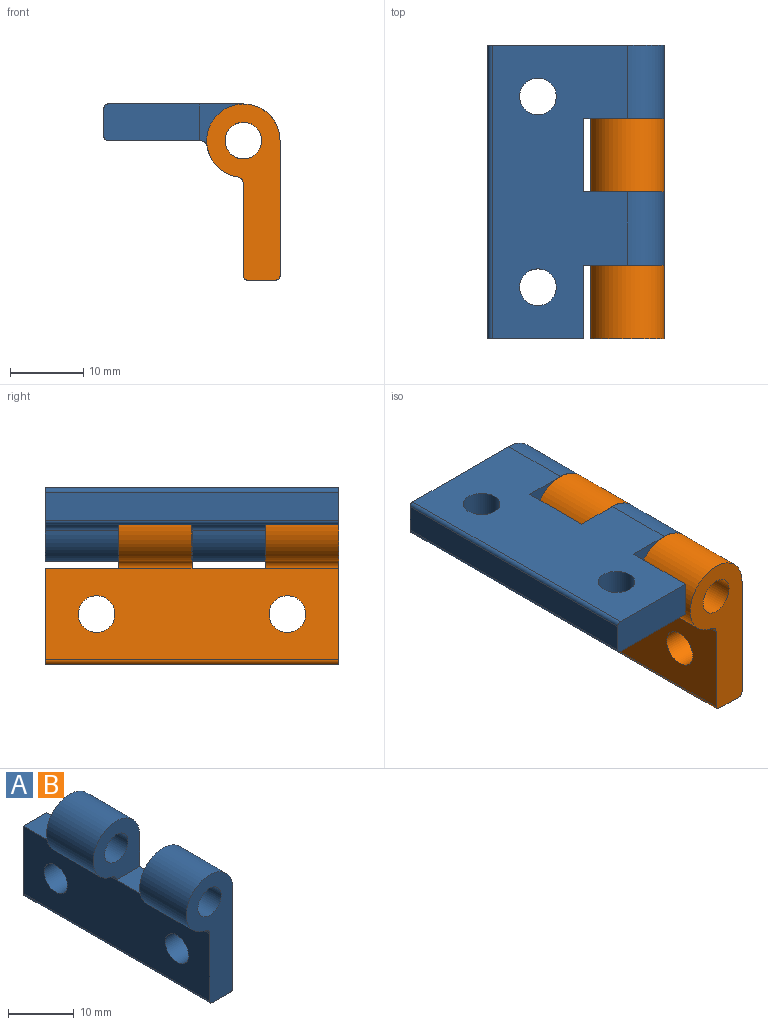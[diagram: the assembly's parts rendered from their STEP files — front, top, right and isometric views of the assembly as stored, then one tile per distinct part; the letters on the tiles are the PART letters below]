
ASSEMBLY  parts=2 mates=1
PART A: 20 faces, bbox 10x40x24 mm
  f0: cylinder r=1mm len=10mm, axis (0,1,0), area 14mm2, adj f2,f5,f13,f16
  f1: plane 40x18.45mm, normal (1,0,0), area 580.4mm2, adj f2,f3,f8,f9,f11,f12,f13,f14
  f2: cylinder r=5mm len=10mm, axis (0,1,0), area 227.2mm2, adj f0,f1,f13,f16
  f3: plane 13.08x5mm, normal (0,1,0), area 65.3mm2, adj f1,f5,f6,f7,f8,f12
  f4: cylinder r=1mm len=10mm, axis (0,1,0), area 14mm2, adj f5,f9,f11,f15
  f5: plane 40x12.53mm, normal (-1,0,0), area 462.1mm2, adj f0,f3,f4,f6,f11,f12,f14,f18
  f6: cylinder r=0.55mm len=40mm, axis (0,1,0), area 34.6mm2, adj f3,f5,f7,f11
  f7: plane 40x3.9mm, normal (0,0,-1), area 156mm2, adj f3,f6,f8,f11
  f8: cylinder r=0.55mm len=40mm, axis (0,1,0), area 34.6mm2, adj f1,f3,f7,f11
  f9: cylinder r=5mm len=10mm, axis (0,1,0), area 227.2mm2, adj f1,f4,f11,f15
  f10: cylinder r=2.5mm len=10mm, axis (0,1,0), area 157.1mm2, adj f11,f15
  f11: plane 24x10mm, normal (0,-1,0), area 134.3mm2, adj f1,f4,f5,f6,f7,f8,f9,f10
  f12: plane 10x5mm, normal (0,0,1), area 50mm2, adj f1,f3,f5,f13
  f13: plane 10.92x10mm, normal (0,1,0), area 69mm2, adj f0,f1,f2,f12,f17
  f14: plane 10x5mm, normal (0,0,1), area 50mm2, adj f1,f5,f15,f16
  f15: plane 10.92x10mm, normal (0,1,0), area 69mm2, adj f1,f4,f9,f10,f14
  f16: plane 10.92x10mm, normal (0,-1,0), area 69mm2, adj f0,f1,f2,f14,f17
  f17: cylinder r=2.5mm len=10mm, axis (0,1,0), area 157.1mm2, adj f13,f16
  f18: cylinder r=2.5mm len=5mm, axis (-1,0,0), area 78.5mm2, adj f1,f5
  f19: cylinder r=2.5mm len=5mm, axis (-1,0,0), area 78.5mm2, adj f1,f5
PART B: same geometry as A
PLACE A rot(axis=(-0.71,0,-0.71),180deg) t=(-62.73,-49.68,22.08)mm
PLACE B t=(-43.73,-9.68,3.08)mm fixed
MATE revolute A.f10 <-> B.f10  axis (0,-1,0) through (-43.73,-29.68,22.08)mm
